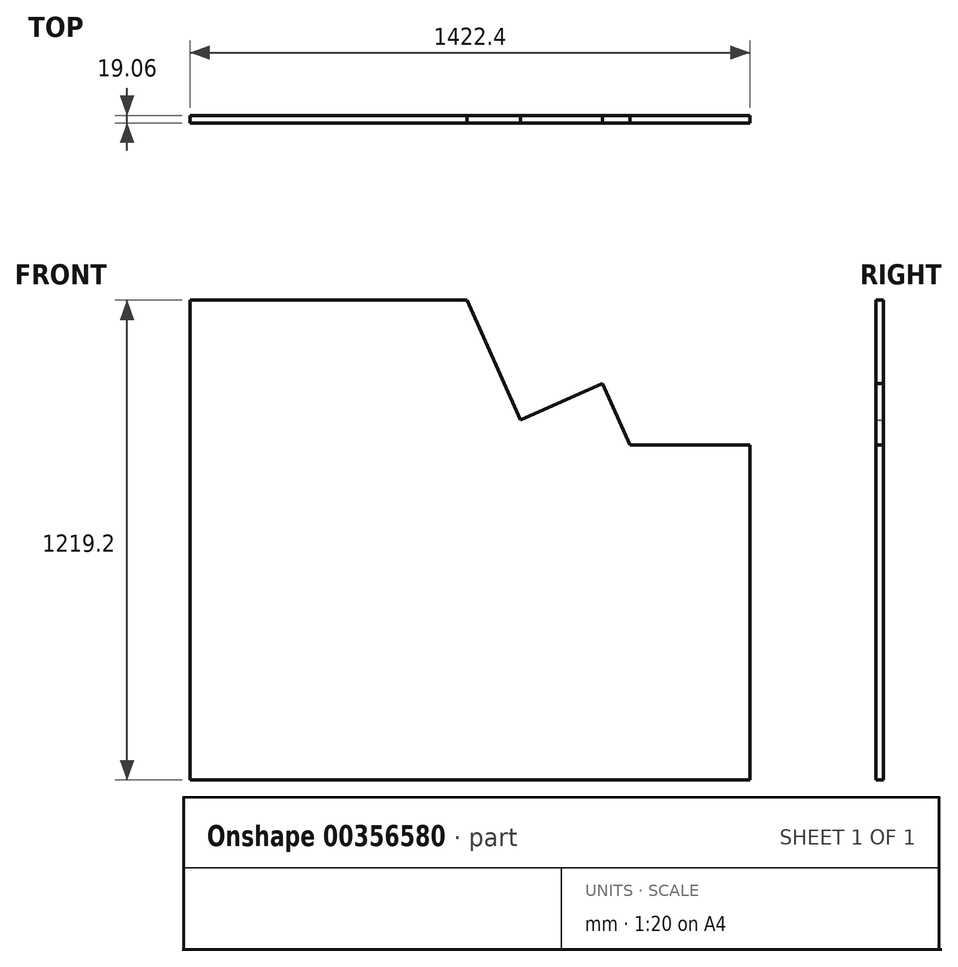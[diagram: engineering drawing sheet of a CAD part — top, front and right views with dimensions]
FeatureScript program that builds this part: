
annotation { "Feature Type Name" : "Feature", "Feature Type Description" : "" }
export const myFeature = defineFeature(function(context is Context, id is Id, definition is map)
    precondition{}
    {
        {
            var Q0;
            Q0=qCreatedBy(makeId("Front.planeOp"),FACE);
            var sketch = newSketch(context, id + "F0", { "sketchPlane" : qUnion([Q0])});
            skLineSegment(sketch, "E0.bottom", {"start": v(-868.76, 430.15) * mm, "end": v(-164.75, 430.15) * mm});
            skLineSegment(sketch, "E0.top", {"start": v(-868.76, -789.05) * mm, "end": v(553.64, -789.05) * mm});
            skLineSegment(sketch, "E0.left", {"start": v(-868.76, 430.15) * mm, "end": v(-868.76, -789.05) * mm});
            skLineSegment(sketch, "E0.right", {"start": v(553.64, 61.85) * mm, "end": v(553.64, -789.05) * mm});
            skPoint(sketch, "E0.middle", {"position": v(-157.56, -179.45) * mm});
            skLineSegment(sketch, "E1", {"start": v(553.64, 61.85) * mm, "end": v(248.84, 61.85) * mm});
            skLineSegment(sketch, "E2", {"start": v(248.84, 61.85) * mm, "end": v(179.49, 218.1) * mm});
            skLineSegment(sketch, "E3", {"start": v(179.49, 218.1) * mm, "end": v(-29.45, 125.35) * mm});
            skLineSegment(sketch, "E4", {"start": v(-29.45, 125.35) * mm, "end": v(-164.75, 430.15) * mm});
            skPoint(sketch, "E5.orphan", {"position": v(553.64, 430.15) * mm});
            skSolve(sketch);
        }
        {
            var Q0;
            Q0=makeQuery(id+"F0.imprint","IMPRINT",FACE,{"disambiguationData":[TD([[makeQuery(id+"F0.imprint","IMPRINT",EDGE,{"derivedFrom":sQuery(id+"F0.wireOp",EDGE,"E0.bottom")}),-1.0]])]});
            extrude(context, id + "F1", {"entities" : qUnion([Q0]), "endBound" : BoundingType.SYMMETRIC, "depth" : 19.05 * mm});
        }
    });
